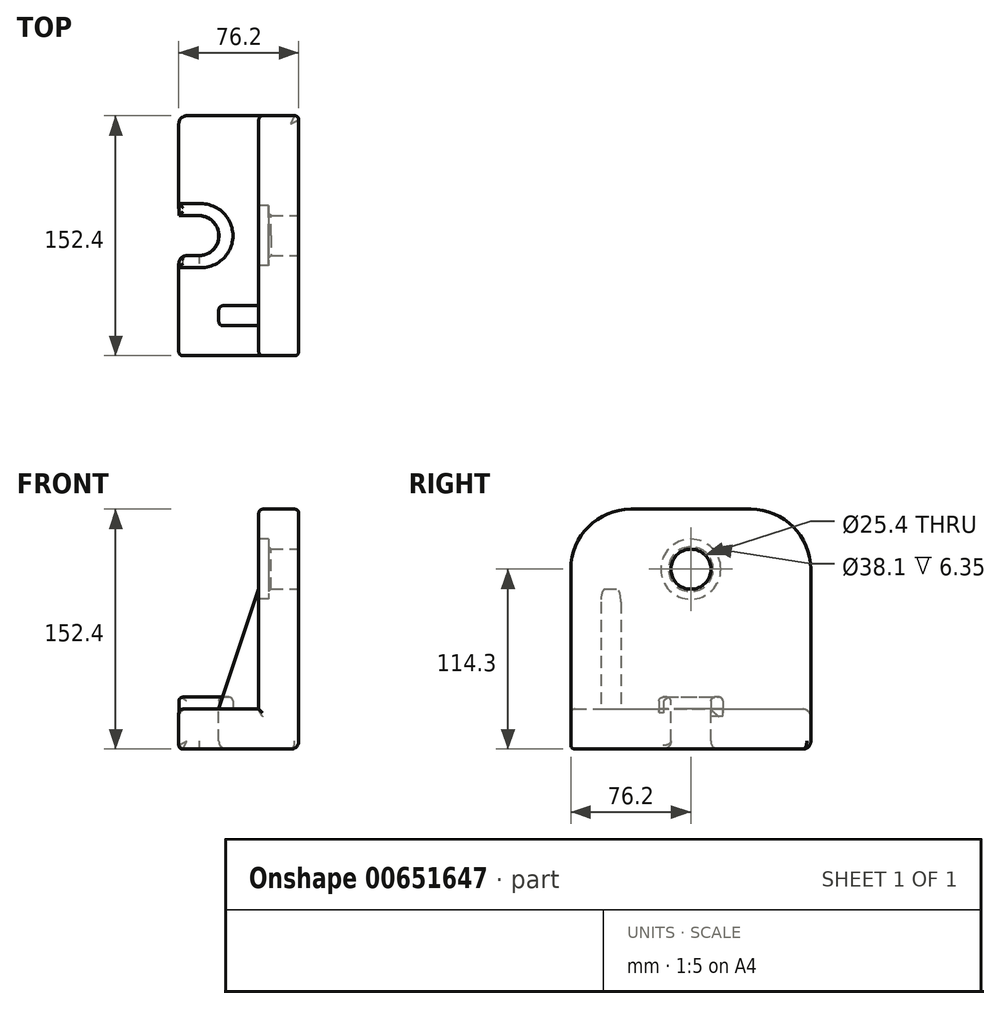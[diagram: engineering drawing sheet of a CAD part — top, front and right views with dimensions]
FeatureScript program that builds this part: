
annotation { "Feature Type Name" : "Feature", "Feature Type Description" : "" }
export const myFeature = defineFeature(function(context is Context, id is Id, definition is map)
    precondition{}
    {
        {
            var Q0;
            Q0=qCreatedBy(makeId("Front.planeOp"),FACE);
            var sketch = newSketch(context, id + "F0", { "sketchPlane" : qUnion([Q0])});
            skLineSegment(sketch, "E0", {"start": v(0, 0) * mm, "end": v(0, 152.4) * mm});
            skLineSegment(sketch, "E1", {"start": v(0, 152.4) * mm, "end": v(-25.4, 152.4) * mm});
            skLineSegment(sketch, "E2", {"start": v(-25.4, 152.4) * mm, "end": v(-25.4, 25.4) * mm});
            skLineSegment(sketch, "E3", {"start": v(-25.4, 25.4) * mm, "end": v(-76.2, 25.4) * mm});
            skLineSegment(sketch, "E4", {"start": v(-76.2, 25.4) * mm, "end": v(-76.2, 0) * mm});
            skLineSegment(sketch, "E5", {"start": v(-76.2, 0) * mm, "end": v(0, 0) * mm});
            skSolve(sketch);
        }
        {
            var Q0;
            Q0 = qSketchRegion(id + "F0", true);
            extrude(context, id + "F1", {"entities" : qUnion([Q0]), "endBound" : BoundingType.SYMMETRIC, "depth" : 152.4 * mm, "offsetDistance" : 25.4 * mm});
        }
        {
            var Q0;
            Q0=qCreatedBy(makeId("Right.planeOp"),FACE);
            var sketch = newSketch(context, id + "F2", { "sketchPlane" : qUnion([Q0])});
            skCircle(sketch, "E6", {"center": v(0, 114.3) * mm, "radius": 12.7 * mm});
            skSolve(sketch);
        }
        {
            var Q0;
            Q0 = qSketchRegion(id + "F2", true);
            extrude(context, id + "F3", {"entities" : qUnion([Q0]), "operationType" : NewBodyOperationType.REMOVE, "endBound" : BoundingType.THROUGH_ALL, "oppositeDirection" : true, "depth" : 25.4 * mm, "offsetDistance" : 25.4 * mm});
        }
        {
            var Q0;
            Q0=makeQuery(id+"F1.opExtrude","SWEPT_FACE",FACE,{"disambiguationData":[OSD([sQuery(id+"F0.wireOp",EDGE,"E3")])]});
            var sketch = newSketch(context, id + "F4", { "sketchPlane" : qUnion([Q0])});
            skLineSegment(sketch, "E7", {"start": v(-76.2, 12.7) * mm, "end": v(-63.5, 12.7) * mm});
            skLineSegment(sketch, "E8", {"start": v(-76.2, -12.7) * mm, "end": v(-63.5, -12.7) * mm});
            skArc(sketch, "E9", {"start": v(-63.5, -12.7) * mm, "mid": v(-50.8, 0) * mm, "end": v(-63.5, 12.7) * mm});
            skSolve(sketch);
        }
        {
            var Q0;
            {var subQ0=sQuery(id+"F4.wireOp",EDGE,"E7");Q0=makeQuery(id+"F4.imprint","IMPRINT",FACE,{"disambiguationData":[TD([[makeQuery(id+"F4.imprint","IMPRINT",EDGE,{"derivedFrom":subQ0}),-1.0]])]});}
            extrude(context, id + "F5", {"entities" : qUnion([Q0]), "operationType" : NewBodyOperationType.REMOVE, "endBound" : BoundingType.THROUGH_ALL, "oppositeDirection" : true, "depth" : 25.4 * mm, "offsetDistance" : 25.4 * mm});
        }
        {
            var Q0;
            Q0=makeQuery(id+"F1.opExtrude","CAP_EDGE",EDGE,{"disambiguationData":[OSD([sQuery(id+"F0.wireOp",EDGE,"E1")])],"isStart":false});
            var Q1;
            Q1=makeQuery(id+"F1.opExtrude","CAP_EDGE",EDGE,{"disambiguationData":[OSD([sQuery(id+"F0.wireOp",EDGE,"E1")])],"isStart":true});
            fillet(context, id + "F6", {"entities" : qUnion([Q0, Q1]), "radius" : 38.1 * mm, "tangentPropagation" : true, "allowEdgeOverflow" : false});
        }
        {
            var Q0;
            Q0=makeQuery(id+"F1.opExtrude","SWEPT_FACE",FACE,{"disambiguationData":[OSD([sQuery(id+"F0.wireOp",EDGE,"E2")])]});
            var sketch = newSketch(context, id + "F7", { "sketchPlane" : qUnion([Q0])});
            skCircle(sketch, "E10", {"center": v(0, 114.3) * mm, "radius": 19.05 * mm});
            skSolve(sketch);
        }
        {
            var Q0;
            Q0 = qSketchRegion(id + "F7", true);
            extrude(context, id + "F8", {"entities" : qUnion([Q0]), "operationType" : NewBodyOperationType.REMOVE, "oppositeDirection" : true, "depth" : 6.35 * mm, "offsetDistance" : 25.4 * mm});
        }
        {
            var Q0;
            Q0=qCreatedBy(makeId("Front.planeOp"),FACE);
            cPlane(context, id + "F9", {"entities" : qUnion([Q0]), "cplaneType" : CPlaneType.OFFSET, "offset" : 44.45 * mm, "width" : 152.4 * mm, "height" : 152.4 * mm});
        }
        {
            var Q0;
            Q0=qCreatedBy(id+"F9.planeOp",FACE);
            var sketch = newSketch(context, id + "F10", { "sketchPlane" : qUnion([Q0])});
            skLineSegment(sketch, "E11.0", {"start": v(-25.4, 25.4) * mm, "end": v(-50.8, 25.4) * mm});
            skLineSegment(sketch, "E12.0", {"start": v(-25.4, 101.6) * mm, "end": v(-25.4, 25.4) * mm});
            skLineSegment(sketch, "E13", {"start": v(-50.8, 25.4) * mm, "end": v(-25.4, 101.6) * mm});
            skPoint(sketch, "E14.orphan", {"position": v(-76.2, 25.4) * mm});
            skPoint(sketch, "E15.orphan", {"position": v(-25.4, 114.3) * mm});
            skSolve(sketch);
        }
        {
            var Q0;
            Q0=makeQuery(id+"F10.imprint","IMPRINT",FACE,{"disambiguationData":[TD([[makeQuery(id+"F10.imprint","IMPRINT",EDGE,{"derivedFrom":sQuery(id+"F10.wireOp",EDGE,"E11.0")}),-1.0]])]});
            extrude(context, id + "F11", {"entities" : qUnion([Q0]), "operationType" : NewBodyOperationType.ADD, "depth" : 12.7 * mm, "offsetDistance" : 25.4 * mm});
        }
        {
            var Q0;
            Q0=makeQuery(id+"F8.boolean.opBoolean","INTERSECT",EDGE,{"derivedFrom":[makeQuery(id+"F3.boolean.opBoolean","COPY",FACE,{"derivedFrom":makeQuery(id+"F3.opExtrude","SWEPT_FACE",FACE,{"disambiguationData":[OSD([sQuery(id+"F2.wireOp",EDGE,"E6")])]})}),makeQuery(id+"F8.opExtrude","CAP_FACE",FACE,{"disambiguationData":[OSD([sQuery(id+"F7.wireOp",EDGE,"E10")])],"isStart":false})]});
            var Q1;
            Q1=makeQuery(id+"F8.boolean.opBoolean","COPY",EDGE,{"derivedFrom":makeQuery(id+"F8.opExtrude","CAP_EDGE",EDGE,{"disambiguationData":[OSD([sQuery(id+"F7.wireOp",EDGE,"E10")])],"isStart":true})});
            chamfer(context, id + "F12", {"entities" : qUnion([Q0, Q1]), "width" : 1.52 * mm, "tangentPropagation" : true});
        }
        {
            var Q0;
            Q0=qCreatedBy(makeId("Top.planeOp"),FACE);
            var sketch = newSketch(context, id + "F13", { "sketchPlane" : qUnion([Q0])});
            skLineSegment(sketch, "E16", {"start": v(-76.14, 20.4) * mm, "end": v(-62.17, 20.4) * mm});
            skLineSegment(sketch, "E17", {"start": v(-76.14, 20.4) * mm, "end": v(-76.14, 12.77) * mm});
            skLineSegment(sketch, "E18", {"start": v(-76.14, 12.77) * mm, "end": v(-63.44, 12.77) * mm});
            skLineSegment(sketch, "E19", {"start": v(-76.18, -12.66) * mm, "end": v(-76.18, -20.28) * mm});
            skLineSegment(sketch, "E20", {"start": v(-76.18, -12.66) * mm, "end": v(-63.48, -12.66) * mm});
            skArc(sketch, "E21", {"start": v(-63.44, 12.77) * mm, "mid": v(-50.72, 0.04) * mm, "end": v(-63.48, -12.66) * mm});
            skLineSegment(sketch, "E22", {"start": v(-76.18, -20.28) * mm, "end": v(-62.2, -20.28) * mm});
            skArc(sketch, "E23", {"start": v(-62.17, 20.4) * mm, "mid": v(-41.83, 0.04) * mm, "end": v(-62.2, -20.28) * mm});
            skSolve(sketch);
        }
        {
            var Q0;
            Q0 = qSketchRegion(id + "F13", true);
            extrude(context, id + "F14", {"entities" : qUnion([Q0]), "operationType" : NewBodyOperationType.ADD, "depth" : 33.02 * mm, "offsetDistance" : 25.4 * mm});
        }
        {
            var Q0;
            Q0=makeQuery(id+"F11.opExtrude","CAP_EDGE",EDGE,{"disambiguationData":[OSD([sQuery(id+"F10.wireOp",EDGE,"E13")])],"isStart":false});
            var Q1;
            Q1=makeQuery(id+"F11.opExtrude","CAP_EDGE",EDGE,{"disambiguationData":[OSD([sQuery(id+"F10.wireOp",EDGE,"E13")])],"isStart":true});
            var Q2;
            Q2=makeQuery(id+"FNTyJo9aofI2l5p_1.1.F11.opExtrude","CAP_EDGE",EDGE,{"disambiguationData":[OSD([sQuery(id+"F10.wireOp",EDGE,"E13")])],"isStart":true});
            var Q3;
            Q3=makeQuery(id+"FNTyJo9aofI2l5p_1.1.F11.opExtrude","CAP_EDGE",EDGE,{"disambiguationData":[OSD([sQuery(id+"F10.wireOp",EDGE,"E13")])],"isStart":false});
            var Q4;
            Q4=makeQuery(id+"F11.opExtrude","SWEPT_EDGE",EDGE,{"disambiguationData":[OSD([sQuery(id+"F10.wireOp",EDGE,"E12.0"),sQuery(id+"F10.wireOp",EDGE,"E13")])]});
            var Q5;
            Q5=makeQuery(id+"F11.opExtrude","SWEPT_EDGE",EDGE,{"disambiguationData":[OSD([sQuery(id+"F10.wireOp",EDGE,"E11.0"),sQuery(id+"F10.wireOp",EDGE,"E13")])]});
            var Q6;
            Q6=makeQuery(id+"FNTyJo9aofI2l5p_1.1.F11.opExtrude","CAP_EDGE",EDGE,{"disambiguationData":[OSD([sQuery(id+"F10.wireOp",EDGE,"E12.0")])],"isStart":true});
            var Q7;
            Q7=makeQuery(id+"FNTyJo9aofI2l5p_1.1.F11.opExtrude","CAP_EDGE",EDGE,{"disambiguationData":[OSD([sQuery(id+"F10.wireOp",EDGE,"E11.0")])],"isStart":true});
            var Q8;
            Q8=makeQuery(id+"FNTyJo9aofI2l5p_1.1.F11.opExtrude","SWEPT_EDGE",EDGE,{"disambiguationData":[OSD([sQuery(id+"F10.wireOp",EDGE,"E12.0"),sQuery(id+"F10.wireOp",EDGE,"E13")])]});
            var Q9;
            Q9=makeQuery(id+"F1.opExtrude","CAP_EDGE",EDGE,{"disambiguationData":[OSD([sQuery(id+"F0.wireOp",EDGE,"E3")])],"isStart":false});
            var Q10;
            Q10=makeQuery(id+"F1.opExtrude","CAP_EDGE",EDGE,{"disambiguationData":[OSD([sQuery(id+"F0.wireOp",EDGE,"E4")])],"isStart":false});
            var Q11;
            Q11=makeQuery(id+"F1.opExtrude","CAP_FACE",FACE,{"disambiguationData":[OSD([sQuery(id+"F0.wireOp",EDGE,"E0"),sQuery(id+"F0.wireOp",EDGE,"E1"),sQuery(id+"F0.wireOp",EDGE,"E2"),sQuery(id+"F0.wireOp",EDGE,"E3"),sQuery(id+"F0.wireOp",EDGE,"E4"),sQuery(id+"F0.wireOp",EDGE,"E5")])],"isStart":false});
            var Q12;
            Q12=makeQuery(id+"F1.opExtrude","CAP_EDGE",EDGE,{"disambiguationData":[OSD([sQuery(id+"F0.wireOp",EDGE,"E2")])],"isStart":false});
            var Q13;
            {var subQ0=sQuery(id+"F0.wireOp",EDGE,"E4");var subQ1=sQuery(id+"F0.wireOp",EDGE,"E3");Q13=makeQuery(id+"F5.boolean.opBoolean","SPLIT",EDGE,{"disambiguationData":[TD([makeQuery(id+"F5.opExtrude","SWEPT_FACE",FACE,{"disambiguationData":[OSD([sQuery(id+"F4.wireOp",EDGE,"E8")])]})])],"derivedFrom":makeQuery(id+"F1.opExtrude","SWEPT_EDGE",EDGE,{"disambiguationData":[OSD([subQ1,subQ0])]})});}
            var Q14;
            Q14=makeQuery(id+"F14.opExtrude","CAP_EDGE",EDGE,{"disambiguationData":[OSD([sQuery(id+"F13.wireOp",EDGE,"E19")])],"isStart":false});
            var Q15;
            {var subQ1=sQuery(id+"F0.wireOp",EDGE,"E4");Q15=makeQuery(id+"F5.boolean.opBoolean","SPLIT",FACE,{"disambiguationData":[TD([makeQuery(id+"F5.opExtrude","SWEPT_FACE",FACE,{"disambiguationData":[OSD([sQuery(id+"F4.wireOp",EDGE,"E8")])]})])],"derivedFrom":makeQuery(id+"F1.opExtrude","SWEPT_FACE",FACE,{"disambiguationData":[OSD([subQ1])]})});}
            var Q16;
            Q16=makeQuery(id+"F14.opExtrude","CAP_EDGE",EDGE,{"disambiguationData":[OSD([sQuery(id+"F13.wireOp",EDGE,"E17")])],"isStart":false});
            var Q17;
            Q17=makeQuery(id+"F14.opExtrude","CAP_EDGE",EDGE,{"disambiguationData":[OSD([sQuery(id+"F13.wireOp",EDGE,"E21")])],"isStart":false});
            var Q18;
            Q18=makeQuery(id+"F14.opExtrude","CAP_EDGE",EDGE,{"disambiguationData":[OSD([sQuery(id+"F13.wireOp",EDGE,"E18")])],"isStart":false});
            var Q19;
            Q19=makeQuery(id+"F14.opExtrude","CAP_EDGE",EDGE,{"disambiguationData":[OSD([sQuery(id+"F13.wireOp",EDGE,"E22")])],"isStart":false});
            var Q20;
            Q20=makeQuery(id+"F14.opExtrude","CAP_EDGE",EDGE,{"disambiguationData":[OSD([sQuery(id+"F13.wireOp",EDGE,"E23")])],"isStart":false});
            var Q21;
            Q21=makeQuery(id+"F14.opExtrude","CAP_EDGE",EDGE,{"disambiguationData":[OSD([sQuery(id+"F13.wireOp",EDGE,"E16")])],"isStart":false});
            var Q22;
            Q22=makeQuery(id+"F14.opExtrude","CAP_EDGE",EDGE,{"disambiguationData":[OSD([sQuery(id+"F13.wireOp",EDGE,"E20")])],"isStart":false});
            var Q23;
            Q23=makeQuery(id+"F5.boolean.opBoolean","COPY",EDGE,{"derivedFrom":makeQuery(id+"F5.opExtrude","CAP_EDGE",EDGE,{"disambiguationData":[OSD([sQuery(id+"F4.wireOp",EDGE,"E7")])],"isStart":true})});
            fillet(context, id + "F15", {"entities" : qUnion([Q0, Q1, Q2, Q3, Q4, Q5, Q6, Q7, Q8, Q9, Q10, Q11, Q12, Q13, Q14, Q15, Q16, Q17, Q18, Q19, Q20, Q21, Q22, Q23]), "radius" : 2.54 * mm, "tangentPropagation" : true, "allowEdgeOverflow" : false});
        }
        {
            var Q0;
            {var subQ0=sQuery(id+"F0.wireOp",EDGE,"E4");var subQ1=sQuery(id+"F0.wireOp",EDGE,"E3");Q0=makeQuery(id+"F5.boolean.opBoolean","SPLIT",EDGE,{"disambiguationData":[TD([makeQuery(id+"F5.opExtrude","SWEPT_FACE",FACE,{"disambiguationData":[OSD([sQuery(id+"F4.wireOp",EDGE,"E7")])]})])],"derivedFrom":makeQuery(id+"F1.opExtrude","SWEPT_EDGE",EDGE,{"disambiguationData":[OSD([subQ1,subQ0])]})});}
            var Q1;
            Q1=makeQuery(id+"F1.opExtrude","CAP_EDGE",EDGE,{"disambiguationData":[OSD([sQuery(id+"F0.wireOp",EDGE,"E3")])],"isStart":true});
            var Q2;
            {var subQ1=sQuery(id+"F0.wireOp",EDGE,"E4");Q2=makeQuery(id+"F5.boolean.opBoolean","SPLIT",FACE,{"disambiguationData":[TD([makeQuery(id+"F5.opExtrude","SWEPT_FACE",FACE,{"disambiguationData":[OSD([sQuery(id+"F4.wireOp",EDGE,"E7")])]})])],"derivedFrom":makeQuery(id+"F1.opExtrude","SWEPT_FACE",FACE,{"disambiguationData":[OSD([subQ1])]})});}
            var Q3;
            Q3=makeQuery(id+"F1.opExtrude","CAP_FACE",FACE,{"disambiguationData":[OSD([sQuery(id+"F0.wireOp",EDGE,"E0"),sQuery(id+"F0.wireOp",EDGE,"E1"),sQuery(id+"F0.wireOp",EDGE,"E2"),sQuery(id+"F0.wireOp",EDGE,"E3"),sQuery(id+"F0.wireOp",EDGE,"E4"),sQuery(id+"F0.wireOp",EDGE,"E5")])],"isStart":true});
            var Q4;
            Q4=makeQuery(id+"F1.opExtrude","SWEPT_EDGE",EDGE,{"disambiguationData":[OSD([sQuery(id+"F0.wireOp",EDGE,"E0"),sQuery(id+"F0.wireOp",EDGE,"E5")])]});
            var Q5;
            Q5=makeQuery(id+"F5.boolean.opBoolean","INTERSECT",EDGE,{"derivedFrom":[makeQuery(id+"F1.opExtrude","SWEPT_FACE",FACE,{"disambiguationData":[OSD([sQuery(id+"F0.wireOp",EDGE,"E5")])]}),makeQuery(id+"F5.opExtrude","SWEPT_FACE",FACE,{"disambiguationData":[OSD([sQuery(id+"F4.wireOp",EDGE,"E9")])]})]});
            var Q6;
            Q6=makeQuery(id+"F5.boolean.opBoolean","INTERSECT",EDGE,{"derivedFrom":[makeQuery(id+"F1.opExtrude","SWEPT_FACE",FACE,{"disambiguationData":[OSD([sQuery(id+"F0.wireOp",EDGE,"E5")])]}),makeQuery(id+"F5.opExtrude","SWEPT_FACE",FACE,{"disambiguationData":[OSD([sQuery(id+"F4.wireOp",EDGE,"E7")])]})]});
            var Q7;
            Q7=makeQuery(id+"F14.opExtrude","CAP_EDGE",EDGE,{"disambiguationData":[OSD([sQuery(id+"F13.wireOp",EDGE,"E20")])],"isStart":true});
            fillet(context, id + "F16", {"entities" : qUnion([Q0, Q1, Q2, Q3, Q4, Q5, Q6, Q7]), "radius" : 5.08 * mm, "tangentPropagation" : true, "allowEdgeOverflow" : false});
        }
    });
